# Revit family: Sanitary_Showers_hansgrohe_26234XXX-Rainfinity-Overhead-shower-360__
name_source: partatom
category: Plumbing Fixtures
revit_build: Autodesk Revit 2018 (Build: 20170223_1515(x64)
units: mm (PartAtom-declared; Revit-internal decimal feet)

## family parameters
Always vertical = No
Cut with Voids When Loaded = No
OmniClass Number = 23.31.17.00
OmniClass Title = Showers
Part Type = Normal
Room Calculation Point = No
Round Connector Dimension = Use Diameter
Shared = No
Work Plane-Based = Yes

## types (6) — shared parameters
Always visible = Yes
BIMobject category = Showers
Default Elevation = 1219.2 mm  [stored 4 ft]
Description = Rainfinity Overhead shower 360 3jet with wall connector
Edition number = 1
IFC Classification = Sanitary Terminal
Manufacturer = Hansgrohe
Manufacturer name = hansgrohe
Material 2 = Hansgrohe - Plastic - Graphite
Model = 26234XXX
OmniClass Code = 23-31 17 00
OmniClass Description = Showers
Product Guid = b5169b9d-b977-4746-a802-850ec91aea31
Product SKU = 26234XXX
Product data url = https://bimobject.com
Product family = Rainfinity
Product group = Overhead showers
Product name = 26234XXX Rainfinity Overhead shower 360 3jet with wall connector
Product url = https://www.hansgrohe.com
QR code = https://bimobject.com
URL = https://www.hansgrohe.com
Weight Net (Kg) = 6,1

## per-type parameters (varying)
| type | Material 1 |
| 000 Chrome | Hansgrohe - Metal - 000 Chrome |
| 140 Brushed Bronze | Hansgrohe - Metal - 140 Brushed Bronze |
| 340 Brushed Black Chrome | Hansgrohe - Metal - 340 Brushed Black Chrome |
| 670 Matt Black | Hansgrohe - Metal - 670 Matt Black |
| 700 Matt White | Hansgrohe - Metal - 700 Matt White |
| 990 Polished Gold Optic | Hansgrohe - Metal - 990 Polished Gold Optic |

note: [stored X ft] marks values corroborated as IEEE doubles in the binary element streams (Revit-internal decimal feet)

## geometry (parser evidence)
native form markers: Sweep x2
no freeform markers — native parametric forms only
